# Revit family: Trap-BottleTrap-ForBasins-Vitra-A45123
name_source: partatom
category: Plumbing Fixtures
revit_build: Autodesk Revit 2017 (Build: 20160225_1515(x64)
units: mm (PartAtom-declared; Revit-internal decimal feet)

## family parameters
Cut with Voids When Loaded = No
Host = Face
OmniClass Number = 23.45.55.17
OmniClass Title = Mixing Faucets
Part Type = Normal
Room Calculation Point = No
Round Connector Dimension = Use Diameter
Shared = Yes

## types (14) — shared parameters
BIMobject category = Sanitary - Taps & Mixers
CW Connection = No
Connection Diameter (mm) = 50 mm  [stored 0.164042 ft]
Default Elevation = 600 mm
Depth(mm) = 315 mm
Description = Bottle Trap For Basins
Design country = Turkey
HW Connection = No
Height(mm) = 144 mm  [stored 0.472441 ft]
IFC Classification = Sanitary Terminal
Manufacturer = Vitra
Manufacturer name = Vitra
Masterformat 2014 Code = 22 40 00
Masterformat 2014 Description = Plumbing Fixtures
MountingType = Wall Mounted
NBS Referans Code = 401425
NBS Referans Description = Traps and strainers
Nominal height = 0.000
Nominal width = 0.000
Number Of Connections = 1 mm  [stored 0.00328084 ft]
OmniClass Code = 23-27 37 00
OmniClass Description = Liquid Traps
Product Properties = Universal
Product Type = T Type Trap
Product certification = https://vitraglobal.com
Product family = Other
Product group = Other Trap
UNSPSC Code = 401425
UNSPSC Description = Traps and strainers
URL = https://vitraglobal.com
Uniclass 1.4 Code = L7218
Uniclass 1.4 Description = Traps for sinks and basins
Uniclass 2.0 Code = PR-62-24
Uniclass 2.0 Description = Drainage Traps
Uniclass 2015 Code = Pr_65_52_25
Uniclass 2015 Name = Drainage traps and accessories
Uniformat II Code = D2010
Uniformat II Description = Plumbing Fixtures
Waste Connection = Yes
Weight Net (kg) = 1,775
Width(mm) = 70 mm
Youtube = https://www.youtube.com
zero-valued in all types: Cost

## per-type parameters (varying)
| type | Article No. (default) | Brand | Coating Material | Color | Installation instructions | Model | Product SKU | Product data url | Product url | Technical description | Warranty Period (Year) |
| Trap-BottleTrap-ForBasins-Vitra-Other(Chrome)-A45123 | A45123 | VitrA | Chrome | Chrome |  | A45123 | A45123 | https://www.bimobject.com | https://www.vitra.com.tr | https://www.vitra.com.tr | 10 Years |
| Trap-BottleTrap-ForBasins-Vitra-Other(Gold)-A4512323 | A4512323 |  | Gold | Gold |  | A4512323 | A4512323 | https://www.vitra.com.tr |  | https://www.vitra.com.tr | 10 Years |
| Trap-BottleTrap-ForBasins-Vitra-Other(Gold)-A4512323EXP | A4512323EXP |  | Gold | Gold |  | A4512323EXP | A4512323EXP | https://www.vitraglobal.com |  | https://www.vitraglobal.com | 5 Years |
| Trap-BottleTrap-ForBasins-Vitra-Other(Gold)-A4512323IND | A4512323EXP |  | Gold | Gold | https://cdn.vitra.com.tr | A4512323EXP | A4512323EXP | https://vitra-india.com |  | https://vitra-india.com | 5 Years |
| Trap-BottleTrap-ForBasins-Vitra-Other(Copper)-A4512326 | A4512326 |  | BrightCopper | Copper |  | A4512326 | A4512326 | https://www.vitraglobal.com |  | https://www.vitraglobal.com | 5 Years |
| Trap-BottleTrap-ForBasins-Vitra-Other(Copper)-A4512326EXP | A4512326EXP |  | BrightCopper | Copper |  | A4512326EXP | A4512326EXP | https://www.vitraglobal.com |  | https://www.vitraglobal.com | 5 Years |
| Trap-BottleTrap-ForBasins-Vitra-Other(BrushedNickel)-A4512334 | A4512334 |  | BrushedNickel | Brushed Nickel |  | A4512334 | A4512334 | https://www.vitra.com.tr |  | https://www.vitra.com.tr | 10 Years |
| Trap-BottleTrap-ForBasins-Vitra-Other(Black)-A4512336 | A4512336 |  | MatteBlack | Black |  | A4512336 | A4512336 | https://www.vitra.com.tr |  | https://www.vitra.com.tr | 10 Years |
| Trap-BottleTrap-ForBasins-Vitra-Other(Chrome)-A45123EXP | A45123EXP |  | Chrome | Chrome |  | A45123EXP | A45123EXP | https://www.vitra.com.tr |  | https://www.vitra.com.tr | 5 Years |
| Trap-BottleTrap-ForBasins-Vitra-Other(Chrome)-A45123IND | A45123IND |  | Chrome | Chrome |  | A45123IND | A45123IND | https://vitra-india.com |  | https://www.vitra.com.tr | 5 Years |
| Trap-BottleTrap-ForBasins-Vitra-Other(White)-A4512399 | A4512399 |  | White | White |  | A4512399 | A4512399 | https://www.vitra.com.tr |  | https://www.vitra.com.tr | 10 Years |
| Trap-BottleTrap-ForBasins-Vitra-Other(White)-A4512399EXP | A4512399EXP |  | White | White |  | A4512399EXP | A4512399EXP | https://www.vitra.com.tr |  | https://www.vitra.com.tr | 5 Years |
| Trap-BottleTrap-ForBasins-Vitra-Other(MatteBlack)-A4512392 | A4512392 |  | MatteBlack | Black |  | A4512392 | A4512392 | https://www.vitra.com.tr |  | https://www.vitra.com.tr | 10 Years |
| Trap-BottleTrap-ForBasins-Vitra-Other(MatteBlack)-A4512392EXP | A4512392EXP |  | MatteBlack | Black |  | A4512392EXP | A4512392EXP | https://www.vitra.com.tr |  | https://www.vitra.com.tr | 5 Years |

note: [stored X ft] marks values corroborated as IEEE doubles in the binary element streams (Revit-internal decimal feet)

## geometry (parser evidence)
native form markers: Sweep x3
no freeform markers — native parametric forms only
